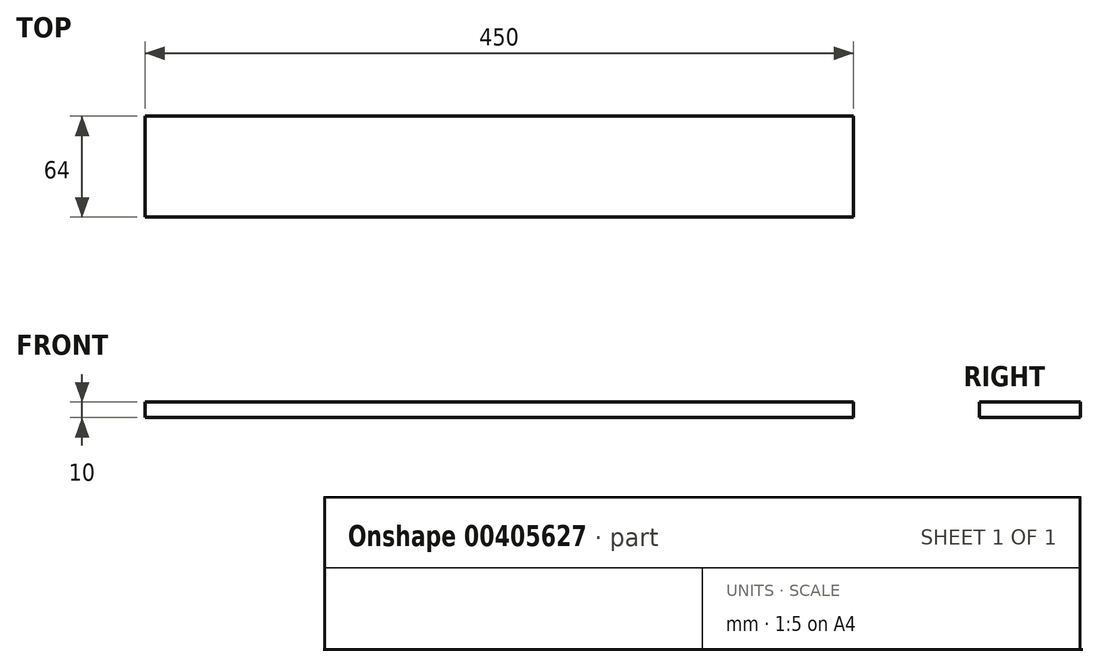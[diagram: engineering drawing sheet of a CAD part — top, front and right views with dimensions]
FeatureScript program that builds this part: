
annotation { "Feature Type Name" : "Feature", "Feature Type Description" : "" }
export const myFeature = defineFeature(function(context is Context, id is Id, definition is map)
    precondition{}
    {
        {
            var Q0;
            Q0=qCreatedBy(makeId("Top.planeOp"),FACE);
            var sketch = newSketch(context, id + "F0", { "sketchPlane" : qUnion([Q0])});
            skLineSegment(sketch, "E0.bottom", {"start": v(-181.1, 14.85) * mm, "end": v(268.9, 14.85) * mm});
            skLineSegment(sketch, "E0.top", {"start": v(-181.1, -49.15) * mm, "end": v(268.9, -49.15) * mm});
            skLineSegment(sketch, "E0.left", {"start": v(-181.1, 14.85) * mm, "end": v(-181.1, -49.15) * mm});
            skLineSegment(sketch, "E0.right", {"start": v(268.9, 14.85) * mm, "end": v(268.9, -49.15) * mm});
            skSolve(sketch);
        }
        {
            var Q0;
            Q0=makeQuery(id+"F0.imprint","IMPRINT",FACE,{"disambiguationData":[TD([[makeQuery(id+"F0.imprint","IMPRINT",EDGE,{"derivedFrom":sQuery(id+"F0.wireOp",EDGE,"E0.bottom")}),-1.0]])]});
            extrude(context, id + "F1", {"entities" : qUnion([Q0]), "depth" : 10 * mm});
        }
    });
